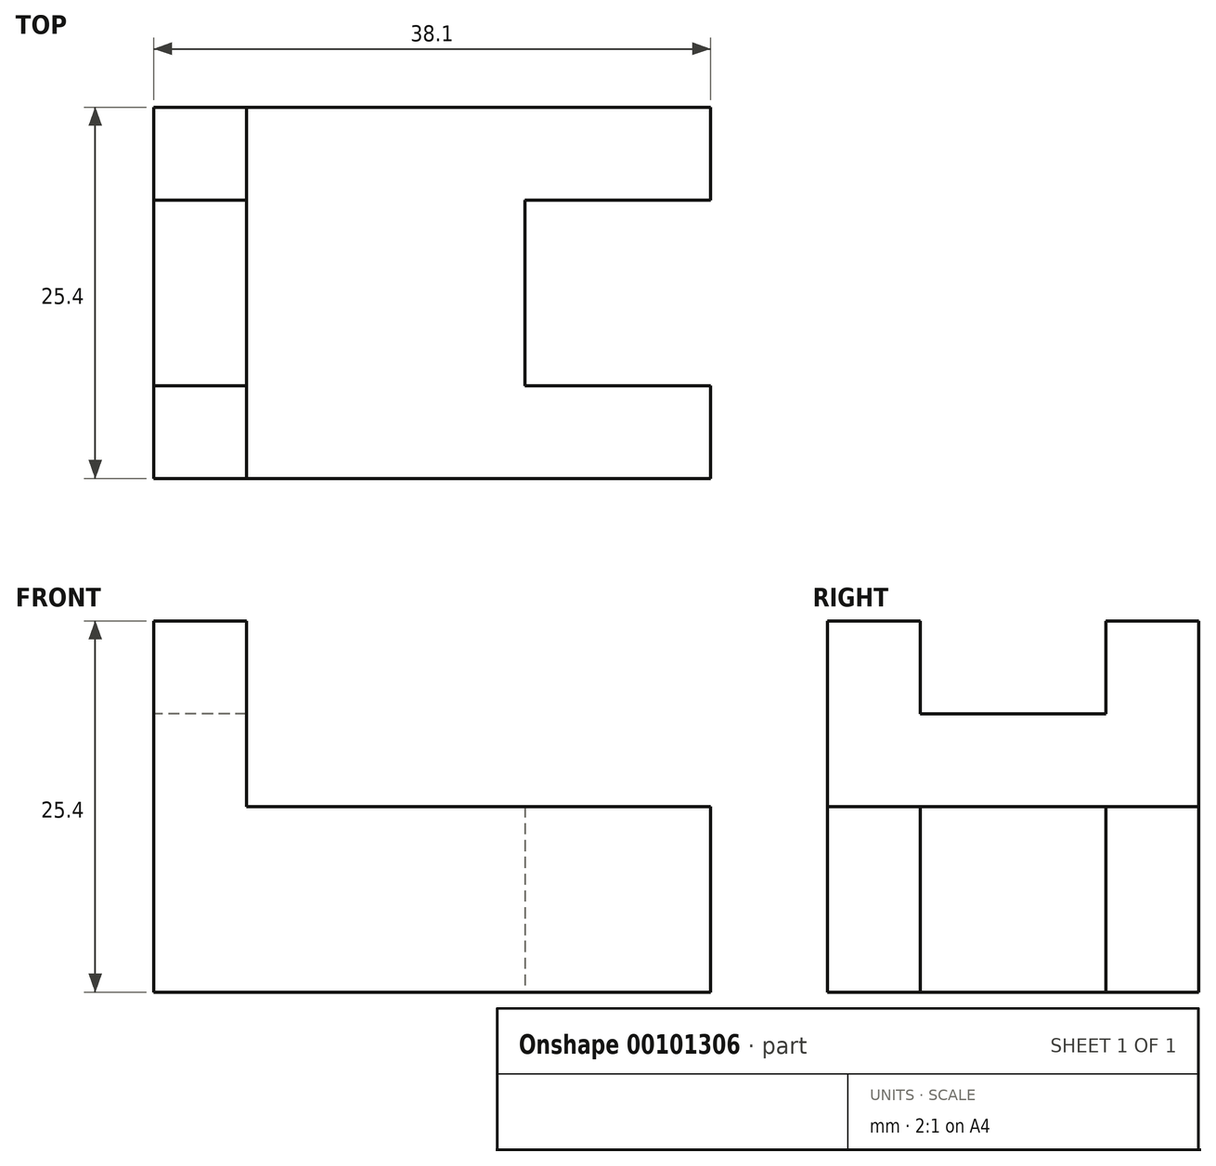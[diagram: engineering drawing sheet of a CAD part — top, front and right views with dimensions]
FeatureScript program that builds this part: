
annotation { "Feature Type Name" : "Feature", "Feature Type Description" : "" }
export const myFeature = defineFeature(function(context is Context, id is Id, definition is map)
    precondition{}
    {
        {
            var Q0;
            Q0=qCreatedBy(makeId("Top.planeOp"),FACE);
            var sketch = newSketch(context, id + "F0", { "sketchPlane" : qUnion([Q0])});
            skLineSegment(sketch, "E0", {"start": v(0, 0) * mm, "end": v(0, 6.35) * mm});
            skLineSegment(sketch, "E1", {"start": v(0, 6.35) * mm, "end": v(-12.7, 6.35) * mm});
            skLineSegment(sketch, "E2", {"start": v(-12.7, 6.35) * mm, "end": v(-12.7, 19.05) * mm});
            skLineSegment(sketch, "E3", {"start": v(-12.7, 19.05) * mm, "end": v(0, 19.05) * mm});
            skLineSegment(sketch, "E4", {"start": v(0, 19.05) * mm, "end": v(0, 25.4) * mm});
            skLineSegment(sketch, "E5", {"start": v(0, 25.4) * mm, "end": v(-38.1, 25.4) * mm});
            skLineSegment(sketch, "E6", {"start": v(-38.1, 25.4) * mm, "end": v(-38.1, 0) * mm});
            skLineSegment(sketch, "E7", {"start": v(-38.1, 0) * mm, "end": v(0, 0) * mm});
            skSolve(sketch);
        }
        {
            var Q0;
            Q0 = qSketchRegion(id + "F0", true);
            extrude(context, id + "F1", {"entities" : qUnion([Q0]), "depth" : 12.7 * mm});
        }
        {
            var Q0;
            Q0=makeQuery(id+"F1.opExtrude","SWEPT_FACE",FACE,{"disambiguationData":[OSD([sQuery(id+"F0.wireOp",EDGE,"E6")])]});
            var sketch = newSketch(context, id + "F2", { "sketchPlane" : qUnion([Q0])});
            skLineSegment(sketch, "E8", {"start": v(-25.4, 0) * mm, "end": v(-25.4, 25.4) * mm});
            skLineSegment(sketch, "E9", {"start": v(-25.4, 25.4) * mm, "end": v(-19.05, 25.4) * mm});
            skLineSegment(sketch, "E10", {"start": v(-19.05, 25.4) * mm, "end": v(-19.05, 19.05) * mm});
            skLineSegment(sketch, "E11", {"start": v(-19.05, 19.05) * mm, "end": v(-6.35, 19.05) * mm});
            skLineSegment(sketch, "E12", {"start": v(-6.35, 19.05) * mm, "end": v(-6.35, 25.4) * mm});
            skLineSegment(sketch, "E13", {"start": v(-6.35, 25.4) * mm, "end": v(0, 25.4) * mm});
            skLineSegment(sketch, "E14", {"start": v(0, 25.4) * mm, "end": v(0, 0) * mm});
            skLineSegment(sketch, "E15", {"start": v(0, 0) * mm, "end": v(-25.4, 0) * mm});
            skSolve(sketch);
        }
        {
            var Q0;
            {var subQ1=sQuery(id+"F2.wireOp",EDGE,"E9");Q0=makeQuery(id+"F2.imprint","IMPRINT",FACE,{"disambiguationData":[TD([[makeQuery(id+"F2.imprint","IMPRINT",EDGE,{"derivedFrom":subQ1}),-1.0]])]});}
            extrude(context, id + "F3", {"entities" : qUnion([Q0]), "operationType" : NewBodyOperationType.ADD, "oppositeDirection" : true, "depth" : 6.35 * mm});
        }
    });
